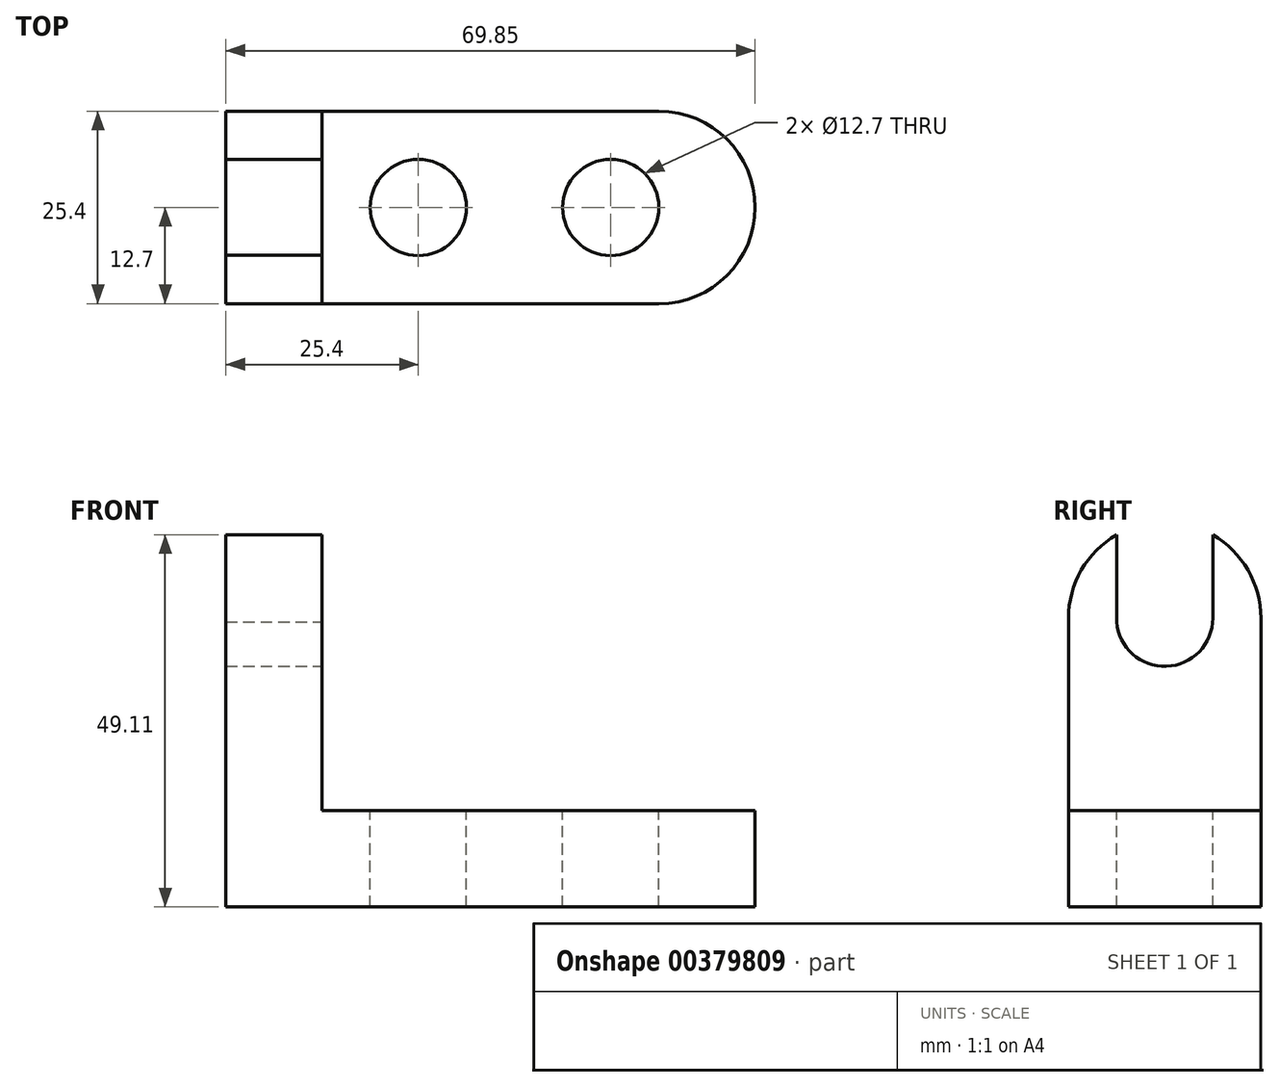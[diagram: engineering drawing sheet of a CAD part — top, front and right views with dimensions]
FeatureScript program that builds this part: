
annotation { "Feature Type Name" : "Feature", "Feature Type Description" : "" }
export const myFeature = defineFeature(function(context is Context, id is Id, definition is map)
    precondition{}
    {
        {
            var Q0;
            Q0=qCreatedBy(makeId("Front.planeOp"),FACE);
            var sketch = newSketch(context, id + "F0", { "sketchPlane" : qUnion([Q0])});
            skLineSegment(sketch, "E0.bottom", {"start": v(0, 50.8) * mm, "end": v(69.85, 50.8) * mm});
            skLineSegment(sketch, "E0.top", {"start": v(0, 0) * mm, "end": v(69.85, 0) * mm});
            skLineSegment(sketch, "E0.left", {"start": v(0, 50.8) * mm, "end": v(0, 0) * mm});
            skLineSegment(sketch, "E0.right", {"start": v(69.85, 50.8) * mm, "end": v(69.85, 0) * mm});
            skLineSegment(sketch, "E1", {"start": v(12.7, 50.8) * mm, "end": v(12.7, 12.7) * mm});
            skLineSegment(sketch, "E2", {"start": v(12.7, 12.7) * mm, "end": v(69.85, 12.7) * mm});
            skSolve(sketch);
        }
        {
            var Q0;
            {var subQ1=sQuery(id+"F0.wireOp",EDGE,"E0.top");Q0=makeQuery(id+"F0.imprint","IMPRINT",FACE,{"disambiguationData":[TD([[makeQuery(id+"F0.imprint","IMPRINT",EDGE,{"derivedFrom":subQ1}),1.0]])]});}
            extrude(context, id + "F1", {"entities" : qUnion([Q0]), "depth" : 25.4 * mm});
        }
        {
            var Q0;
            Q0=makeQuery(id+"F1.opExtrude","SWEPT_FACE",FACE,{"disambiguationData":[OSD([sQuery(id+"F0.wireOp",EDGE,"E2")])]});
            var sketch = newSketch(context, id + "F2", { "sketchPlane" : qUnion([Q0])});
            skCircle(sketch, "E3", {"center": v(25.4, -12.7) * mm, "radius": 6.35 * mm});
            skCircle(sketch, "E4", {"center": v(50.8, -12.7) * mm, "radius": 6.35 * mm});
            skLineSegment(sketch, "E5", {"start": v(53.21, 0) * mm, "end": v(57.15, 0) * mm});
            skLineSegment(sketch, "E6", {"start": v(69.85, -12.7) * mm, "end": v(69.85, -12.7) * mm});
            skLineSegment(sketch, "E7", {"start": v(57.15, -25.4) * mm, "end": v(53.21, -25.4) * mm});
            skPoint(sketch, "E8.visualSharp", {"position": v(69.85, 0) * mm});
            skArc(sketch, "E8.filletArc", {"start": v(69.85, -12.7) * mm, "mid": v(66.13, -3.72) * mm, "end": v(57.15, 0) * mm});
            skPoint(sketch, "E9.visualSharp", {"position": v(69.85, -25.4) * mm});
            skArc(sketch, "E9.filletArc", {"start": v(57.15, -25.4) * mm, "mid": v(66.13, -21.68) * mm, "end": v(69.85, -12.7) * mm});
            skSolve(sketch);
        }
        {
            var Q0;
            Q0=makeQuery(id+"F2.imprint","IMPRINT",FACE,{"disambiguationData":[TD([[makeQuery(id+"F2.imprint","IMPRINT",EDGE,{"derivedFrom":sQuery(id+"F2.wireOp",EDGE,"E3")}),1.0]])]});
            var Q1;
            {var subQ0=sQuery(id+"F2.wireOp",EDGE,"E9.filletArc");Q1=makeQuery(id+"F2.imprint","IMPRINT",FACE,{"disambiguationData":[TD([[makeQuery(id+"F2.imprint","IMPRINT",EDGE,{"derivedFrom":subQ0}),-1.0]])]});}
            var Q2;
            Q2=makeQuery(id+"F2.imprint","IMPRINT",FACE,{"disambiguationData":[TD([[makeQuery(id+"F2.imprint","IMPRINT",EDGE,{"derivedFrom":sQuery(id+"F2.wireOp",EDGE,"E4")}),1.0]])]});
            var Q3;
            {var subQ0=sQuery(id+"F2.wireOp",EDGE,"E8.filletArc");Q3=makeQuery(id+"F2.imprint","IMPRINT",FACE,{"disambiguationData":[TD([[makeQuery(id+"F2.imprint","IMPRINT",EDGE,{"derivedFrom":subQ0}),-1.0]])]});}
            extrude(context, id + "F3", {"entities" : qUnion([Q0, Q1, Q2, Q3]), "operationType" : NewBodyOperationType.REMOVE, "oppositeDirection" : true, "depth" : 25.4 * mm});
        }
        {
            var Q0;
            Q0=makeQuery(id+"F1.opExtrude","SWEPT_FACE",FACE,{"disambiguationData":[OSD([sQuery(id+"F0.wireOp",EDGE,"E1")])]});
            var sketch = newSketch(context, id + "F4", { "sketchPlane" : qUnion([Q0])});
            skLineSegment(sketch, "E10", {"start": v(-12.7, 50.8) * mm, "end": v(-12.7, 50.8) * mm});
            skLineSegment(sketch, "E11", {"start": v(0, 39.26) * mm, "end": v(0, 38.1) * mm});
            skLineSegment(sketch, "E12", {"start": v(-25.4, 38.1) * mm, "end": v(-25.4, 39.26) * mm});
            skPoint(sketch, "E13.visualSharp", {"position": v(0, 50.8) * mm});
            skArc(sketch, "E13.filletArc", {"start": v(0, 38.1) * mm, "mid": v(-3.72, 47.08) * mm, "end": v(-12.7, 50.8) * mm});
            skPoint(sketch, "E14.visualSharp", {"position": v(-25.4, 50.8) * mm});
            skArc(sketch, "E14.filletArc", {"start": v(-12.7, 50.8) * mm, "mid": v(-21.68, 47.08) * mm, "end": v(-25.4, 38.1) * mm});
            skSolve(sketch);
        }
        {
            var Q0;
            {var subQ0=sQuery(id+"F4.wireOp",EDGE,"E11");Q0=makeQuery(id+"F4.imprint","IMPRINT",FACE,{"disambiguationData":[TD([[makeQuery(id+"F4.imprint","IMPRINT",EDGE,{"derivedFrom":subQ0}),-1.0]])]});}
            var Q1;
            {var subQ0=sQuery(id+"F4.wireOp",EDGE,"E12");Q1=makeQuery(id+"F4.imprint","IMPRINT",FACE,{"disambiguationData":[TD([[makeQuery(id+"F4.imprint","IMPRINT",EDGE,{"derivedFrom":subQ0}),1.0]])]});}
            extrude(context, id + "F5", {"entities" : qUnion([Q0, Q1]), "operationType" : NewBodyOperationType.REMOVE, "oppositeDirection" : true, "depth" : 25.4 * mm});
        }
        {
            var Q0;
            Q0=makeQuery(id+"F1.opExtrude","SWEPT_FACE",FACE,{"disambiguationData":[OSD([sQuery(id+"F0.wireOp",EDGE,"E1")])]});
            var sketch = newSketch(context, id + "F6", { "sketchPlane" : qUnion([Q0])});
            skCircle(sketch, "E15", {"center": v(-12.7, 38.1) * mm, "radius": 6.35 * mm});
            skLineSegment(sketch, "E16", {"start": v(-19.03, 37.64) * mm, "end": v(-19.03, 49.1) * mm});
            skLineSegment(sketch, "E17", {"start": v(-6.35, 38.1) * mm, "end": v(-6.35, 49.1) * mm});
            skSolve(sketch);
        }
        {
            var Q0;
            {var subQ0=sQuery(id+"F6.wireOp",EDGE,"E15");var subQ1=makeQuery(id+"F6.imprint","INTERSECT",VERTEX,{"derivedFrom":[subQ0,sQuery(id+"F6.wireOp",EDGE,"E17")]});Q0=makeQuery(id+"F6.imprint","IMPRINT",FACE,{"disambiguationData":[TD([[makeQuery(id+"F6.imprint","IMPRINT",EDGE,{"disambiguationData":[TD([[subQ1,-1.0]])],"derivedFrom":subQ0}),1.0]])]});}
            var Q1;
            {var subQ0=sQuery(id+"F6.wireOp",EDGE,"E17");Q1=makeQuery(id+"F6.imprint","IMPRINT",FACE,{"disambiguationData":[TD([[makeQuery(id+"F6.imprint","IMPRINT",EDGE,{"derivedFrom":subQ0}),1.0]])]});}
            extrude(context, id + "F7", {"entities" : qUnion([Q0, Q1]), "operationType" : NewBodyOperationType.REMOVE, "oppositeDirection" : true, "depth" : 25.4 * mm});
        }
    });
